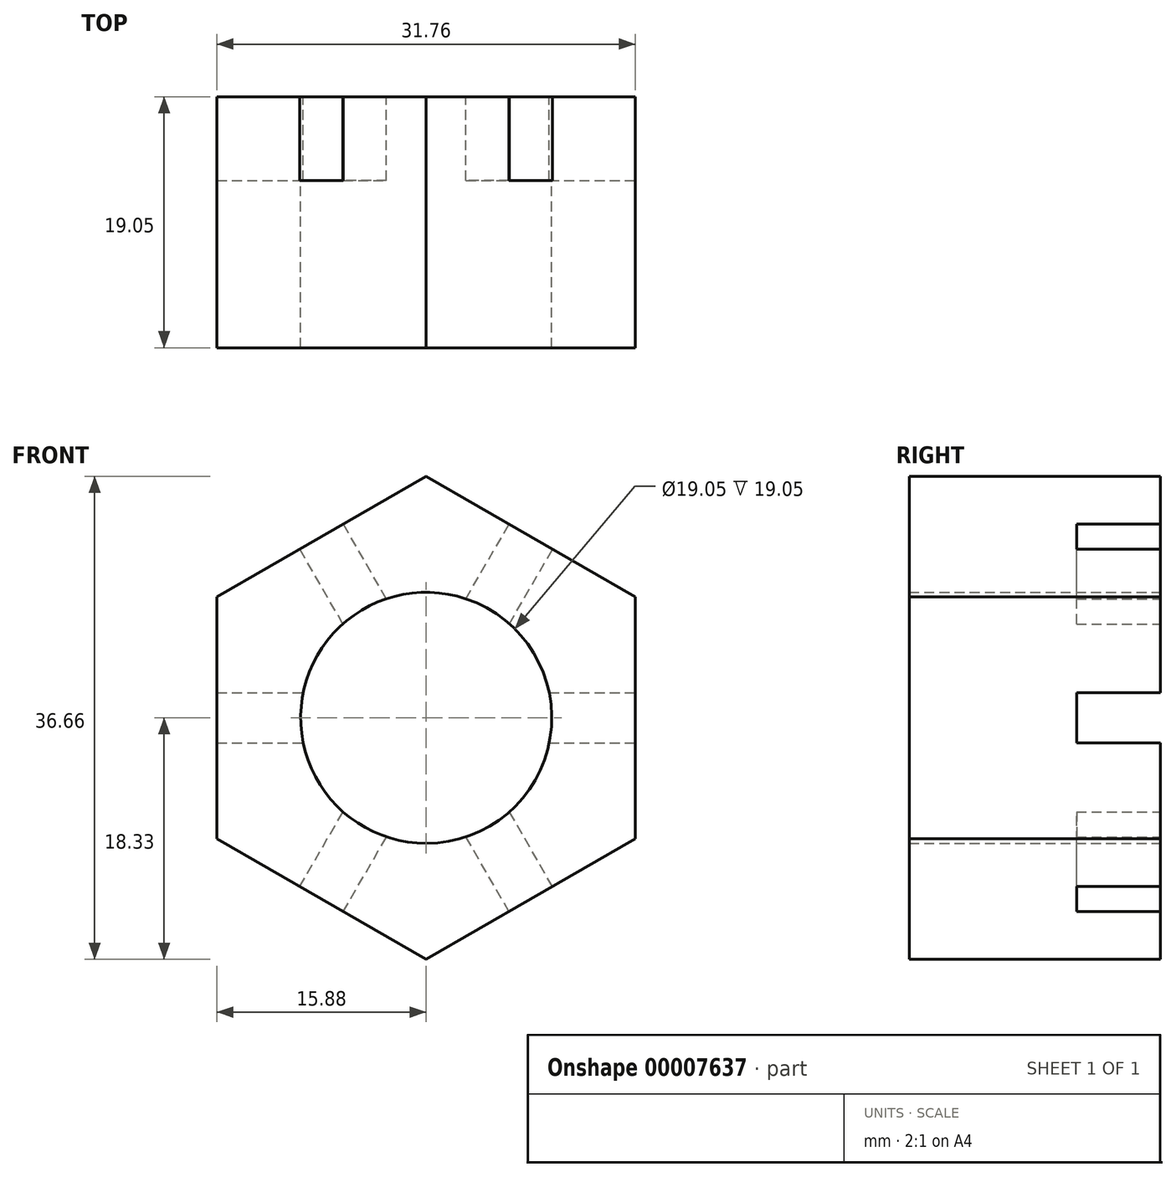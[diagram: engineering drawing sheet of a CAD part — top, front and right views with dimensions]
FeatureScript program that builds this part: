
annotation { "Feature Type Name" : "Feature", "Feature Type Description" : "" }
export const myFeature = defineFeature(function(context is Context, id is Id, definition is map)
    precondition{}
    {
        {
            var Q0;
            Q0=qCreatedBy(makeId("Front.planeOp"),FACE);
            var sketch = newSketch(context, id + "F0", { "sketchPlane" : qUnion([Q0])});
            skCircle(sketch, "E0.cCircle", {"center": v(0, 0) * mm, "radius": 15.88 * mm, "construction": true});
            skLineSegment(sketch, "E0.0", {"start": v(-15.88, -9.17) * mm, "end": v(-15.88, 9.17) * mm});
            skLineSegment(sketch, "E0.1", {"start": v(-15.88, 9.17) * mm, "end": v(0, 18.33) * mm});
            skLineSegment(sketch, "E0.2", {"start": v(0, 18.33) * mm, "end": v(15.88, 9.17) * mm});
            skLineSegment(sketch, "E0.3", {"start": v(15.88, 9.17) * mm, "end": v(15.88, -9.17) * mm});
            skLineSegment(sketch, "E0.4", {"start": v(15.88, -9.17) * mm, "end": v(0, -18.33) * mm});
            skLineSegment(sketch, "E0.5", {"start": v(0, -18.33) * mm, "end": v(-15.88, -9.17) * mm});
            skPoint(sketch, "E0.0.midPoint", {"position": v(-15.88, 0) * mm});
            skCircle(sketch, "E1", {"center": v(0, 0) * mm, "radius": 9.53 * mm});
            skSolve(sketch);
        }
        {
            var Q0;
            Q0 = qSketchRegion(id + "F0", true);
            extrude(context, id + "F1", {"entities" : qUnion([Q0]), "depth" : 19.05 * mm});
        }
        {
            var Q0;
            Q0=makeQuery(id+"F1.opExtrude","SWEPT_FACE",FACE,{"disambiguationData":[OSD([sQuery(id+"F0.wireOp",EDGE,"E0.1")])]});
            var sketch = newSketch(context, id + "F2", { "sketchPlane" : qUnion([Q0])});
            skLineSegment(sketch, "E2.bottom", {"start": v(-1.9, -6.35) * mm, "end": v(1.9, -6.35) * mm});
            skLineSegment(sketch, "E2.top", {"start": v(-1.9, 0) * mm, "end": v(1.9, 0) * mm});
            skLineSegment(sketch, "E2.left", {"start": v(-1.9, -6.35) * mm, "end": v(-1.9, 0) * mm});
            skLineSegment(sketch, "E2.right", {"start": v(1.9, -6.35) * mm, "end": v(1.9, 0) * mm});
            skSolve(sketch);
        }
        {
            var Q0;
            Q0 = qSketchRegion(id + "F2", true);
            extrude(context, id + "F3", {"entities" : qUnion([Q0]), "operationType" : NewBodyOperationType.REMOVE, "endBound" : BoundingType.THROUGH_ALL, "oppositeDirection" : true, "depth" : 25.4 * mm});
        }
        {
            var Q0;
            Q0=makeQuery(id+"F1.opExtrude","SWEPT_FACE",FACE,{"disambiguationData":[OSD([sQuery(id+"F0.wireOp",EDGE,"E0.2")])]});
            var sketch = newSketch(context, id + "F4", { "sketchPlane" : qUnion([Q0])});
            skLineSegment(sketch, "E3.bottom", {"start": v(-1.9, 0) * mm, "end": v(1.9, 0) * mm});
            skLineSegment(sketch, "E3.top", {"start": v(-1.9, -6.35) * mm, "end": v(1.9, -6.35) * mm});
            skLineSegment(sketch, "E3.left", {"start": v(-1.9, 0) * mm, "end": v(-1.9, -6.35) * mm});
            skLineSegment(sketch, "E3.right", {"start": v(1.9, 0) * mm, "end": v(1.9, -6.35) * mm});
            skSolve(sketch);
        }
        {
            var Q0;
            Q0 = qSketchRegion(id + "F4", true);
            extrude(context, id + "F5", {"entities" : qUnion([Q0]), "operationType" : NewBodyOperationType.REMOVE, "endBound" : BoundingType.THROUGH_ALL, "oppositeDirection" : true, "depth" : 25.4 * mm});
        }
        {
            var Q0;
            Q0=makeQuery(id+"F1.opExtrude","SWEPT_FACE",FACE,{"disambiguationData":[OSD([sQuery(id+"F0.wireOp",EDGE,"E0.3")])]});
            var sketch = newSketch(context, id + "F6", { "sketchPlane" : qUnion([Q0])});
            skLineSegment(sketch, "E4.bottom", {"start": v(0, 1.9) * mm, "end": v(-6.35, 1.9) * mm});
            skLineSegment(sketch, "E4.top", {"start": v(0, -1.9) * mm, "end": v(-6.35, -1.9) * mm});
            skLineSegment(sketch, "E4.left", {"start": v(0, 1.9) * mm, "end": v(0, -1.9) * mm});
            skLineSegment(sketch, "E4.right", {"start": v(-6.35, 1.9) * mm, "end": v(-6.35, -1.9) * mm});
            skSolve(sketch);
        }
        {
            var Q0;
            Q0 = qSketchRegion(id + "F6", true);
            extrude(context, id + "F7", {"entities" : qUnion([Q0]), "operationType" : NewBodyOperationType.REMOVE, "endBound" : BoundingType.THROUGH_ALL, "oppositeDirection" : true, "depth" : 25.4 * mm});
        }
    });
